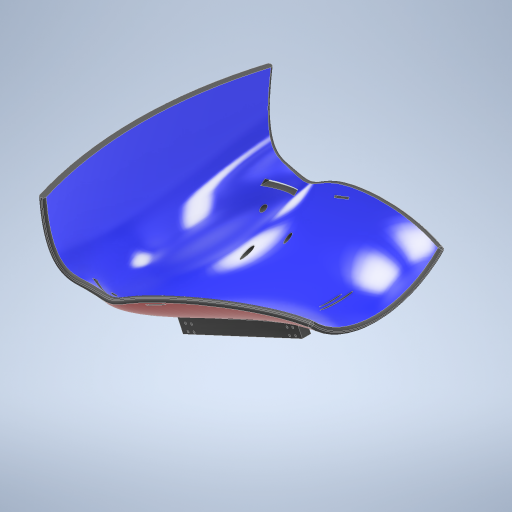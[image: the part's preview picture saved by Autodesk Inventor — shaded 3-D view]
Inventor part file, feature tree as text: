
AUTODESK INVENTOR PART (.ipt)
format: ipt  version: 2024 (Build 280153000, 153)  size: 1,642,496 bytes
history: native  units: in
note: dims shown in document units (in); Inventor stores cm internally (conversion verified against a paired STEP export)
features: extrude x2, sketch x2
ambient origin geometry x8: Origin, YZ Plane, XZ Plane, XY Plane, X Axis, Y Axis, Z Axis, Center Point
bodies: Solid1 (feature_tree), Body1 (feature_tree)
feature tree (4):
  extrude  "Extrusion1"  Depth=0.1969in
  extrude  "Extrusion2"  Depth=0.5906in
  sketch  "Sketch1"  dims[d0=0.1969in d1=0.1969in]
  sketch  "Sketch2"  dims[d2=0.1969in d3=0.5906in d4=0.5906in d5=0.5906in d6=0.1969in d7=0.5906in d8=0.1969in d9=0.1969in d10=0.5906in d11=0.1969in d12=0.1969in d13=0.5906in d14=0.1969in d15=0.5906in d16=0.1969in d17=0.1969in d18=0.5906in d19=0.5906in d20=22.6875in d21=0.0in d22=0.7874in d23=0.7874in d24=0.5512in d25=0.0in d26=0.5in d27=1.9685in]
